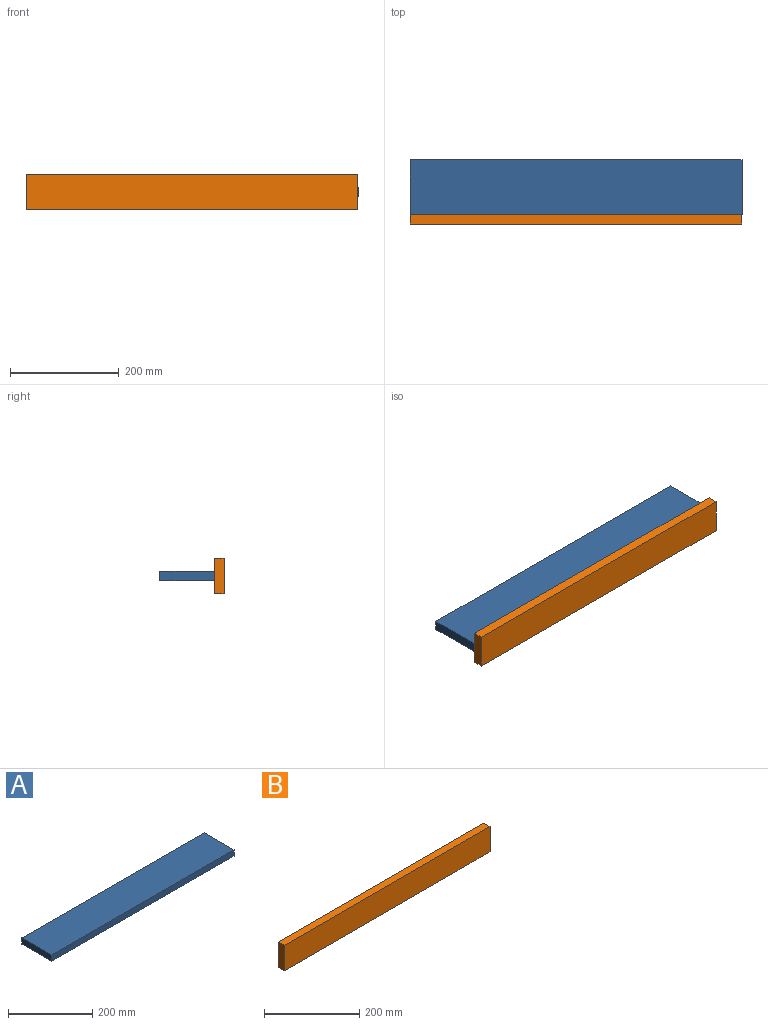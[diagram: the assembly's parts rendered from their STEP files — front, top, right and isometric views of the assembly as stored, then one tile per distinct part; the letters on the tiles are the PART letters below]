
ASSEMBLY  parts=2 mates=2
PART A: 6 faces, bbox 610x100x18 mm
  f0: plane 100x18mm, normal (-1,0,0), area 1800mm2, adj f1,f3,f4,f5
  f1: plane 610x18mm, normal (0,-1,0), area 10980mm2, adj f0,f2,f4,f5
  f2: plane 100x18mm, normal (1,0,0), area 1800mm2, adj f1,f3,f4,f5
  f3: plane 610x18mm, normal (0,1,0), area 10980mm2, adj f0,f2,f4,f5
  f4: plane 610x100mm, normal (0,0,1), area 61000mm2, adj f0,f1,f2,f3
  f5: plane 610x100mm, normal (0,0,-1), area 61000mm2, adj f0,f1,f2,f3
PART B: 6 faces, bbox 610x18x65 mm
  f0: plane 610x18mm, normal (0,0,1), area 10980mm2, adj f1,f3,f4,f5
  f1: plane 65x18mm, normal (-1,0,0), area 1170mm2, adj f0,f2,f4,f5
  f2: plane 610x18mm, normal (0,0,-1), area 10980mm2, adj f1,f3,f4,f5
  f3: plane 65x18mm, normal (1,0,0), area 1170mm2, adj f0,f2,f4,f5
  f4: plane 610x65mm, normal (0,-1,0), area 39650mm2, adj f0,f1,f2,f3
  f5: plane 610x65mm, normal (0,1,0), area 39650mm2, adj f0,f1,f2,f3
PLACE A t=(-315.6,519.59,-174.36)mm
PLACE B t=(-171.64,-698.81,1058.19)mm
MATE planar A.f2 <-> B.f3  axis (1,0,0) through (-627.83,-648.81,-165.36)mm
MATE planar A.f1 <-> B.f5  axis (0,-1,0) through (-932.83,-698.81,-165.36)mm
